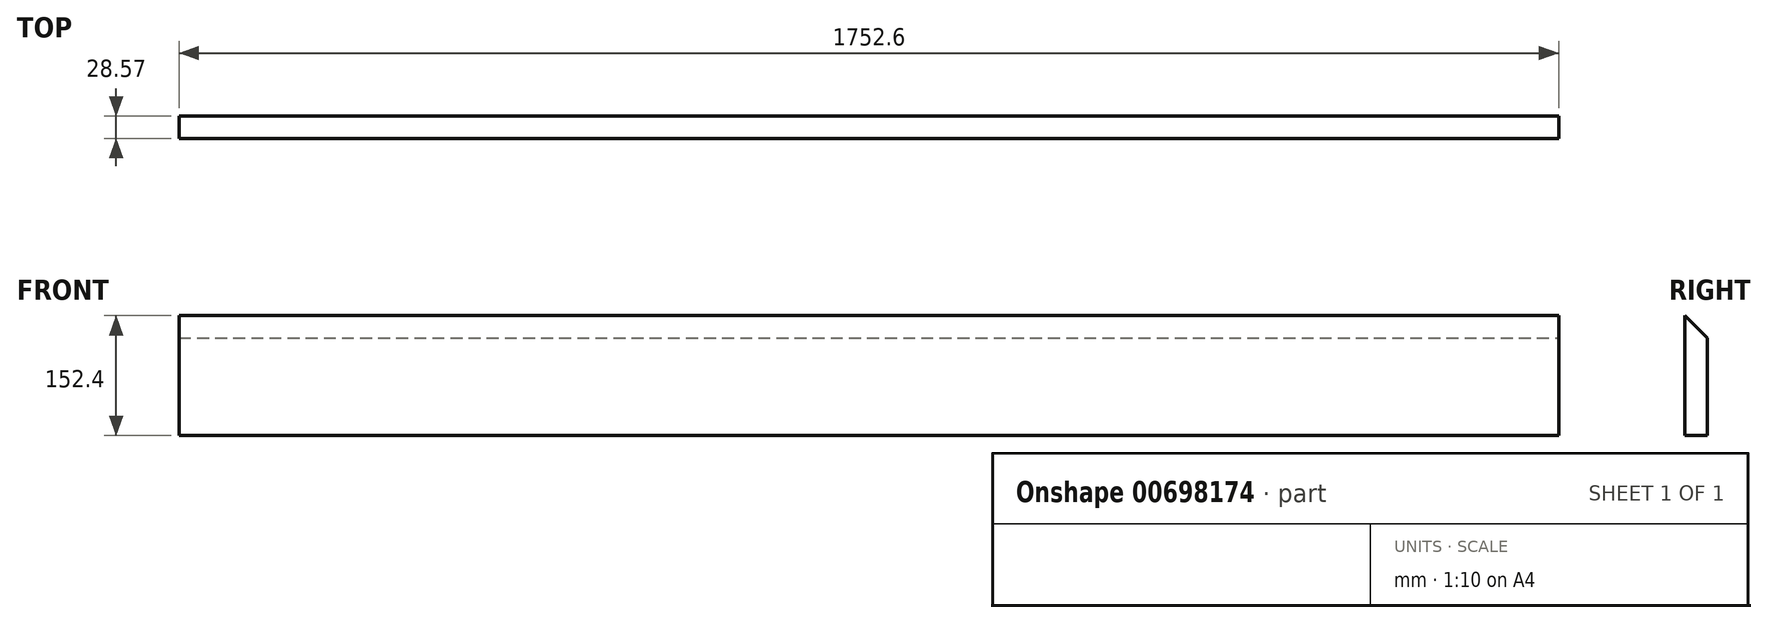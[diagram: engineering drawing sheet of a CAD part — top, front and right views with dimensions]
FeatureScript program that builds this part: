
annotation { "Feature Type Name" : "Feature", "Feature Type Description" : "" }
export const myFeature = defineFeature(function(context is Context, id is Id, definition is map)
    precondition{}
    {
        {
            var Q0;
            Q0=qCreatedBy(makeId("Front.planeOp"),FACE);
            var sketch = newSketch(context, id + "F0", { "sketchPlane" : qUnion([Q0])});
            skLineSegment(sketch, "E0.bottom", {"start": v(876.3, 76.2) * mm, "end": v(-876.3, 76.2) * mm});
            skLineSegment(sketch, "E0.top", {"start": v(876.3, -76.2) * mm, "end": v(-876.3, -76.2) * mm});
            skLineSegment(sketch, "E0.left", {"start": v(876.3, 76.2) * mm, "end": v(876.3, -76.2) * mm});
            skLineSegment(sketch, "E0.right", {"start": v(-876.3, 76.2) * mm, "end": v(-876.3, -76.2) * mm});
            skPoint(sketch, "E0.middle", {"position": v(0, 0) * mm});
            skSolve(sketch);
        }
        {
            var Q0;
            Q0=makeQuery(id+"F0.imprint","IMPRINT",FACE,{"disambiguationData":[TD([[makeQuery(id+"F0.imprint","IMPRINT",EDGE,{"derivedFrom":sQuery(id+"F0.wireOp",EDGE,"E0.bottom")}),1.0]])]});
            extrude(context, id + "F1", {"entities" : qUnion([Q0]), "depth" : 28.57 * mm, "offsetDistance" : 25.4 * mm});
        }
        {
            var Q0;
            Q0=makeQuery(id+"F1.opExtrude","SWEPT_FACE",FACE,{"disambiguationData":[OSD([sQuery(id+"F0.wireOp",EDGE,"E0.left")])]});
            var sketch = newSketch(context, id + "F2", { "sketchPlane" : qUnion([Q0])});
            skLineSegment(sketch, "E1", {"start": v(0, 76.2) * mm, "end": v(0, 47.63) * mm});
            skLineSegment(sketch, "E2", {"start": v(0, 47.63) * mm, "end": v(-28.58, 76.2) * mm});
            skSolve(sketch);
        }
        {
            var Q0;
            Q0=makeQuery(id+"F2.imprint","IMPRINT",FACE,{"disambiguationData":[TD([[makeQuery(id+"F2.imprint","IMPRINT",EDGE,{"derivedFrom":sQuery(id+"F2.wireOp",EDGE,"E1")}),-1.0]])]});
            extrude(context, id + "F3", {"entities" : qUnion([Q0]), "operationType" : NewBodyOperationType.REMOVE, "oppositeDirection" : true, "depth" : 1752.6 * mm, "offsetDistance" : 25.4 * mm});
        }
    });
